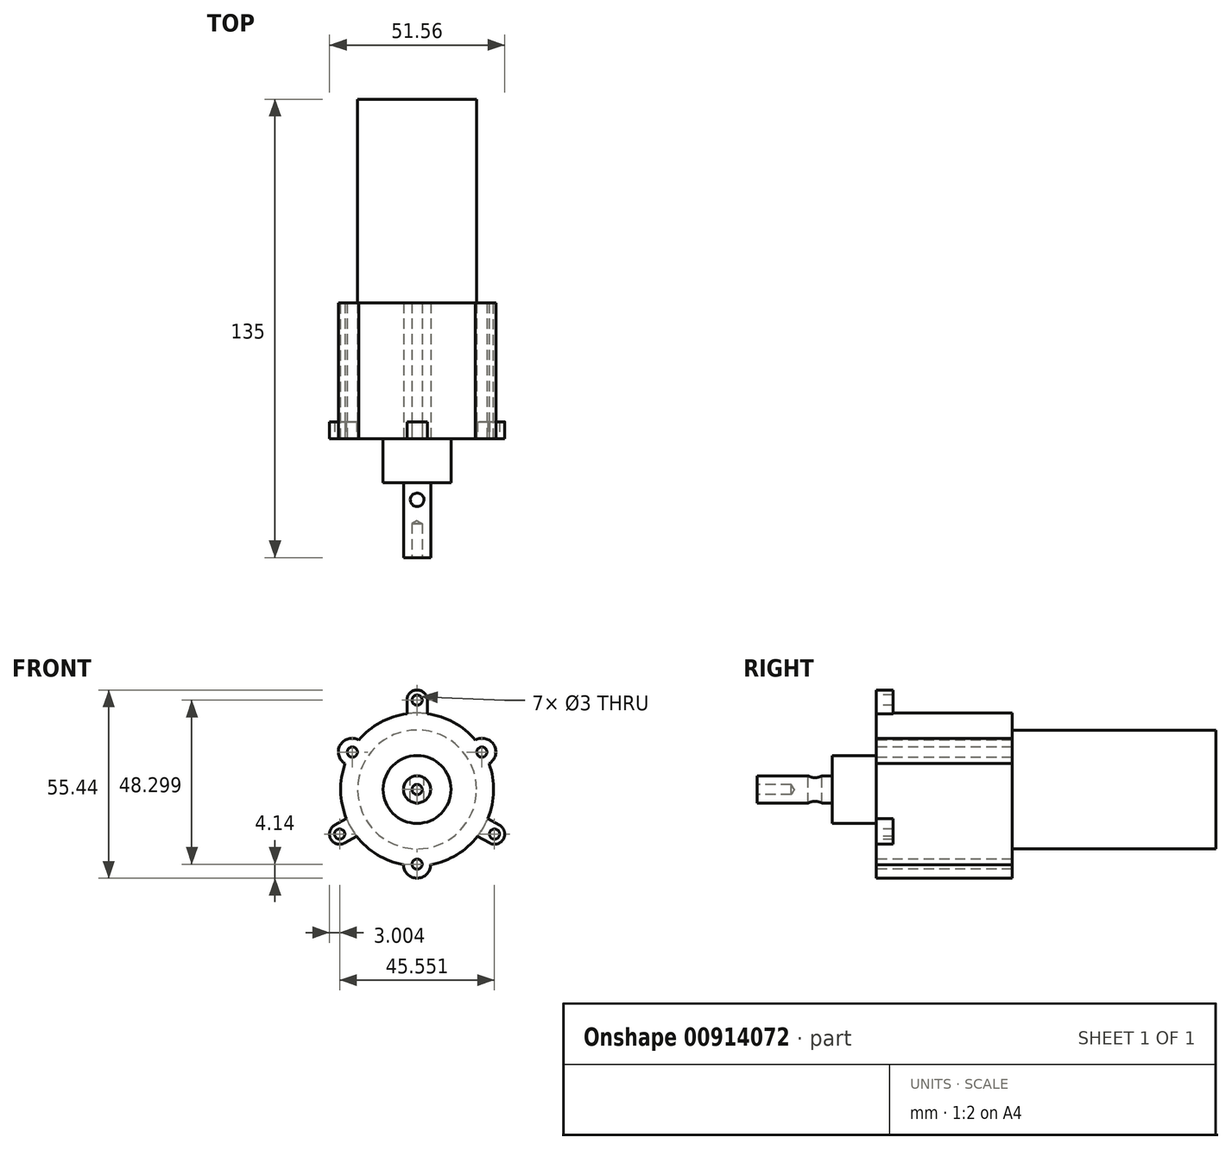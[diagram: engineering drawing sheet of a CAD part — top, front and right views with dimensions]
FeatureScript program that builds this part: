
annotation { "Feature Type Name" : "Feature", "Feature Type Description" : "" }
export const myFeature = defineFeature(function(context is Context, id is Id, definition is map)
    precondition{}
    {
        {
            var Q0;
            Q0=qCreatedBy(makeId("Front.planeOp"),FACE);
            var sketch = newSketch(context, id + "F0", { "sketchPlane" : qUnion([Q0])});
            skCircle(sketch, "E0", {"center": v(0, 0) * mm, "radius": 17.5 * mm});
            skSolve(sketch);
        }
        {
            var Q0;
            Q0=qSketchRegion(id+"F0",true);
            extrude(context, id + "F1", {"entities" : qUnion([Q0]), "depth" : 60 * mm, "offsetDistance" : 25 * mm});
        }
        {
            var Q0;
            Q0=makeQuery(id+"F1.opExtrude","CAP_FACE",FACE,{"disambiguationData":[OSD([sQuery(id+"F0.wireOp",EDGE,"E0")])],"isStart":false});
            var sketch = newSketch(context, id + "F2", { "sketchPlane" : qUnion([Q0])});
            skCircle(sketch, "E1", {"center": v(0, 0) * mm, "radius": 22.5 * mm});
            skSolve(sketch);
        }
        {
            var Q0;
            Q0=qSketchRegion(id+"F2",true);
            extrude(context, id + "F3", {"entities" : qUnion([Q0]), "operationType" : NewBodyOperationType.ADD, "depth" : 40 * mm, "offsetDistance" : 25 * mm});
        }
        {
            var Q0;
            Q0=makeQuery(id+"F3.opExtrude","CAP_FACE",FACE,{"disambiguationData":[OSD([sQuery(id+"F2.wireOp",EDGE,"E1")])],"isStart":false});
            var sketch = newSketch(context, id + "F4", { "sketchPlane" : qUnion([Q0])});
            skLineSegment(sketch, "E2", {"start": v(0, 0) * mm, "end": v(0, -22.5) * mm, "construction": true});
            skLineSegment(sketch, "E3", {"start": v(-4, -22.14) * mm, "end": v(4, -22.14) * mm});
            skArc(sketch, "E4", {"start": v(-4, -22.14) * mm, "mid": v(0, -26.14) * mm, "end": v(4, -22.14) * mm});
            skArc(sketch, "E5.1.0", {"start": v(21.18, 7.6) * mm, "mid": v(22.64, 13.07) * mm, "end": v(17.18, 14.53) * mm});
            skLineSegment(sketch, "E5.1.1", {"start": v(21.18, 7.6) * mm, "end": v(17.18, 14.53) * mm});
            skArc(sketch, "E5.2.0", {"start": v(-17.18, 14.53) * mm, "mid": v(-22.64, 13.07) * mm, "end": v(-21.18, 7.6) * mm});
            skLineSegment(sketch, "E5.2.1", {"start": v(-17.18, 14.53) * mm, "end": v(-21.18, 7.6) * mm});
            skPoint(sketch, "E5.center", {"position": v(0, 0) * mm});
            skSolve(sketch);
        }
        {
            var Q0;
            Q0=qSketchRegion(id+"F4",true);
            extrude(context, id + "F5", {"entities" : qUnion([Q0]), "operationType" : NewBodyOperationType.ADD, "oppositeDirection" : true, "depth" : 40 * mm, "offsetDistance" : 25 * mm});
        }
        {
            var Q0;
            Q0=makeQuery(id+"F5.boolean.opBoolean","MERGE",FACE,{"derivedFrom":[makeQuery(id+"F3.opExtrude","CAP_FACE",FACE,{"disambiguationData":[OSD([sQuery(id+"F2.wireOp",EDGE,"E1")])],"isStart":false}),makeQuery(id+"F5.opExtrude","CAP_FACE",FACE,{"disambiguationData":[OSD([sQuery(id+"F4.wireOp",EDGE,"E3"),sQuery(id+"F4.wireOp",EDGE,"E4")])],"isStart":true})]});
            var sketch = newSketch(context, id + "F6", { "sketchPlane" : qUnion([Q0])});
            skPoint(sketch, "E6", {"position": v(0, -22) * mm});
            skPoint(sketch, "E7.1.0", {"position": v(19.05, 11) * mm});
            skPoint(sketch, "E7.2.0", {"position": v(-19.05, 11) * mm});
            skPoint(sketch, "E7.center", {"position": v(0, 0) * mm});
            skSolve(sketch);
        }
        {
            var Q0;
            Q0=sQuery(id+"F6.wireOp",VERTEX,"E7.2.0");
            var Q1;
            Q1=sQuery(id+"F6.wireOp",VERTEX,"E6");
            var Q2;
            Q2=sQuery(id+"F6.wireOp",VERTEX,"E7.1.0");
            var Q3;
            Q3=makeQuery(id+"F1.opExtrude","SWEPT_BODY",BODY,{"disambiguationData":[OSD([sQuery(id+"F0.wireOp",EDGE,"E0")])]});
            hole(context, id + "F7", {"style" : HoleStyle.SIMPLE, "endStyle" : HoleEndStyle.THROUGH, "holeDiameter" : 3 * mm, "majorDiameter" : 5 * mm, "isTappedThrough" : true, "tappedDepth" : 12 * mm, "tapClearance" : 3, "locations" : qUnion([Q0, Q1, Q2]), "scope" : qUnion([Q3])});
        }
        {
            var Q0;
            Q0=makeQuery(id+"F3.opExtrude","CAP_FACE",FACE,{"disambiguationData":[OSD([sQuery(id+"F2.wireOp",EDGE,"E1")])],"isStart":false});
            var sketch = newSketch(context, id + "F8", { "sketchPlane" : qUnion([Q0])});
            skLineSegment(sketch, "E8", {"start": v(0, 22.5) * mm, "end": v(0, -22.5) * mm, "construction": true});
            skLineSegment(sketch, "E9", {"start": v(-22.5, 0) * mm, "end": v(22.5, 0) * mm, "construction": true});
            skLineSegment(sketch, "E10", {"start": v(-3, 22.3) * mm, "end": v(-3, 26.3) * mm});
            skLineSegment(sketch, "E11", {"start": v(3, 26.3) * mm, "end": v(3, 22.3) * mm});
            skArc(sketch, "E12", {"start": v(3, 26.3) * mm, "mid": v(0, 29.3) * mm, "end": v(-3, 26.3) * mm});
            skLineSegment(sketch, "E13", {"start": v(-3, 22.3) * mm, "end": v(3, 22.3) * mm});
            skCircle(sketch, "E14", {"center": v(0, 26.3) * mm, "radius": 1.5 * mm});
            skArc(sketch, "E15.1.0", {"start": v(-24.28, -10.55) * mm, "mid": v(-25.37, -14.65) * mm, "end": v(-21.28, -15.75) * mm});
            skCircle(sketch, "E15.1.1", {"center": v(-22.78, -13.15) * mm, "radius": 1.5 * mm});
            skLineSegment(sketch, "E15.1.2", {"start": v(-24.28, -10.55) * mm, "end": v(-20.81, -8.55) * mm});
            skLineSegment(sketch, "E15.1.3", {"start": v(-17.81, -13.75) * mm, "end": v(-21.28, -15.75) * mm});
            skLineSegment(sketch, "E15.1.4", {"start": v(-17.81, -13.75) * mm, "end": v(-20.81, -8.55) * mm});
            skArc(sketch, "E15.2.0", {"start": v(21.28, -15.75) * mm, "mid": v(25.37, -14.65) * mm, "end": v(24.28, -10.55) * mm});
            skCircle(sketch, "E15.2.1", {"center": v(22.78, -13.15) * mm, "radius": 1.5 * mm});
            skLineSegment(sketch, "E15.2.2", {"start": v(21.28, -15.75) * mm, "end": v(17.81, -13.75) * mm});
            skLineSegment(sketch, "E15.2.3", {"start": v(20.81, -8.55) * mm, "end": v(24.28, -10.55) * mm});
            skLineSegment(sketch, "E15.2.4", {"start": v(20.81, -8.55) * mm, "end": v(17.81, -13.75) * mm});
            skPoint(sketch, "E15.center", {"position": v(0, 0) * mm});
            skSolve(sketch);
        }
        {
            var Q0;
            Q0=qSketchRegion(id+"F8",true);
            extrude(context, id + "F9", {"entities" : qUnion([Q0]), "operationType" : NewBodyOperationType.ADD, "oppositeDirection" : true, "depth" : 5 * mm, "offsetDistance" : 25 * mm});
        }
        {
            var Q0;
            Q0=makeQuery(id+"F9.boolean.opBoolean","MERGE",FACE,{"derivedFrom":[makeQuery(id+"F5.boolean.opBoolean","MERGE",FACE,{"derivedFrom":[makeQuery(id+"F3.opExtrude","CAP_FACE",FACE,{"disambiguationData":[OSD([sQuery(id+"F2.wireOp",EDGE,"E1")])],"isStart":false}),makeQuery(id+"F5.opExtrude","CAP_FACE",FACE,{"disambiguationData":[OSD([sQuery(id+"F4.wireOp",EDGE,"E3"),sQuery(id+"F4.wireOp",EDGE,"E4")])],"isStart":true}),makeQuery(id+"F5.opExtrude","CAP_FACE",FACE,{"disambiguationData":[OSD([sQuery(id+"F4.wireOp",EDGE,"E5.1.0"),sQuery(id+"F4.wireOp",EDGE,"E5.1.1")])],"isStart":true}),makeQuery(id+"F5.opExtrude","CAP_FACE",FACE,{"disambiguationData":[OSD([sQuery(id+"F4.wireOp",EDGE,"E5.2.0"),sQuery(id+"F4.wireOp",EDGE,"E5.2.1")])],"isStart":true})]}),makeQuery(id+"F9.opExtrude","CAP_FACE",FACE,{"disambiguationData":[OSD([sQuery(id+"F8.wireOp",EDGE,"E10"),sQuery(id+"F8.wireOp",EDGE,"E11"),sQuery(id+"F8.wireOp",EDGE,"E12"),sQuery(id+"F8.wireOp",EDGE,"E13"),sQuery(id+"F8.wireOp",EDGE,"E14")])],"isStart":true}),makeQuery(id+"F9.opExtrude","CAP_FACE",FACE,{"disambiguationData":[OSD([sQuery(id+"F8.wireOp",EDGE,"E15.1.0"),sQuery(id+"F8.wireOp",EDGE,"E15.1.1"),sQuery(id+"F8.wireOp",EDGE,"E15.1.2"),sQuery(id+"F8.wireOp",EDGE,"E15.1.3"),sQuery(id+"F8.wireOp",EDGE,"E15.1.4")])],"isStart":true}),makeQuery(id+"F9.opExtrude","CAP_FACE",FACE,{"disambiguationData":[OSD([sQuery(id+"F8.wireOp",EDGE,"E15.2.0"),sQuery(id+"F8.wireOp",EDGE,"E15.2.1"),sQuery(id+"F8.wireOp",EDGE,"E15.2.2"),sQuery(id+"F8.wireOp",EDGE,"E15.2.3"),sQuery(id+"F8.wireOp",EDGE,"E15.2.4")])],"isStart":true})]});
            var sketch = newSketch(context, id + "F10", { "sketchPlane" : qUnion([Q0])});
            skCircle(sketch, "E16", {"center": v(0, 0) * mm, "radius": 10 * mm});
            skSolve(sketch);
        }
        {
            var Q0;
            Q0=makeQuery(id+"F10.imprint","IMPRINT",FACE,{"disambiguationData":[TD([[makeQuery(id+"F10.imprint","IMPRINT",EDGE,{"derivedFrom":sQuery(id+"F10.wireOp",EDGE,"E16")}),1.0]])]});
            extrude(context, id + "F11", {"entities" : qUnion([Q0]), "operationType" : NewBodyOperationType.ADD, "depth" : 13 * mm, "offsetDistance" : 25 * mm});
        }
        {
            var Q0;
            Q0=makeQuery(id+"F11.opExtrude","CAP_FACE",FACE,{"disambiguationData":[OSD([sQuery(id+"F10.wireOp",EDGE,"E16")])],"isStart":false});
            var sketch = newSketch(context, id + "F12", { "sketchPlane" : qUnion([Q0])});
            skCircle(sketch, "E17", {"center": v(0, 0) * mm, "radius": 4 * mm});
            skSolve(sketch);
        }
        {
            var Q0;
            Q0=makeQuery(id+"F12.imprint","IMPRINT",FACE,{"disambiguationData":[TD([[makeQuery(id+"F12.imprint","IMPRINT",EDGE,{"derivedFrom":sQuery(id+"F12.wireOp",EDGE,"E17")}),1.0]])]});
            var Q1;
            Q1=sQuery(id+"F12.wireOp",EDGE,"E17");
            extrude(context, id + "F13", {"entities" : qUnion([Q0]), "operationType" : NewBodyOperationType.ADD, "surfaceEntities" : qUnion([Q1]), "depth" : 22 * mm, "offsetDistance" : 25 * mm});
        }
        {
            var Q0;
            Q0=makeQuery(id+"F13.opExtrude","CAP_FACE",FACE,{"disambiguationData":[OSD([sQuery(id+"F12.wireOp",EDGE,"E17")])],"isStart":false});
            var sketch = newSketch(context, id + "F14", { "sketchPlane" : qUnion([Q0])});
            skPoint(sketch, "E18", {"position": v(0, 0) * mm});
            skSolve(sketch);
        }
        {
            var Q0;
            Q0=sQuery(id+"F14.wireOp",VERTEX,"E18");
            var Q1;
            Q1=makeQuery(id+"F1.opExtrude","SWEPT_BODY",BODY,{"disambiguationData":[OSD([sQuery(id+"F0.wireOp",EDGE,"E0")])]});
            hole(context, id + "F15", {"style" : HoleStyle.SIMPLE, "endStyle" : HoleEndStyle.BLIND, "holeDiameter" : 3 * mm, "majorDiameter" : 5 * mm, "holeDepth" : 10 * mm, "isTappedThrough" : true, "tappedDepth" : 12 * mm, "tapClearance" : 3, "locations" : qUnion([Q0]), "scope" : qUnion([Q1])});
        }
        {
            var Q0;
            Q0=qCreatedBy(makeId("Top.planeOp"),FACE);
            var sketch = newSketch(context, id + "F16", { "sketchPlane" : qUnion([Q0])});
            skPoint(sketch, "E19", {"position": v(0, -118) * mm});
            skCircle(sketch, "E20", {"center": v(0, -118) * mm, "radius": 2 * mm});
            skSolve(sketch);
        }
        {
            var Q0;
            Q0=qSketchRegion(id+"F16",true);
            var Q1;
            Q1=sQuery(id+"F16.wireOp",EDGE,"E20");
            extrude(context, id + "F17", {"entities" : qUnion([Q0]), "operationType" : NewBodyOperationType.REMOVE, "surfaceEntities" : qUnion([Q1]), "oppositeDirection" : true, "depth" : 25 * mm, "offsetDistance" : 25 * mm, "symmetric" : true});
        }
    });
